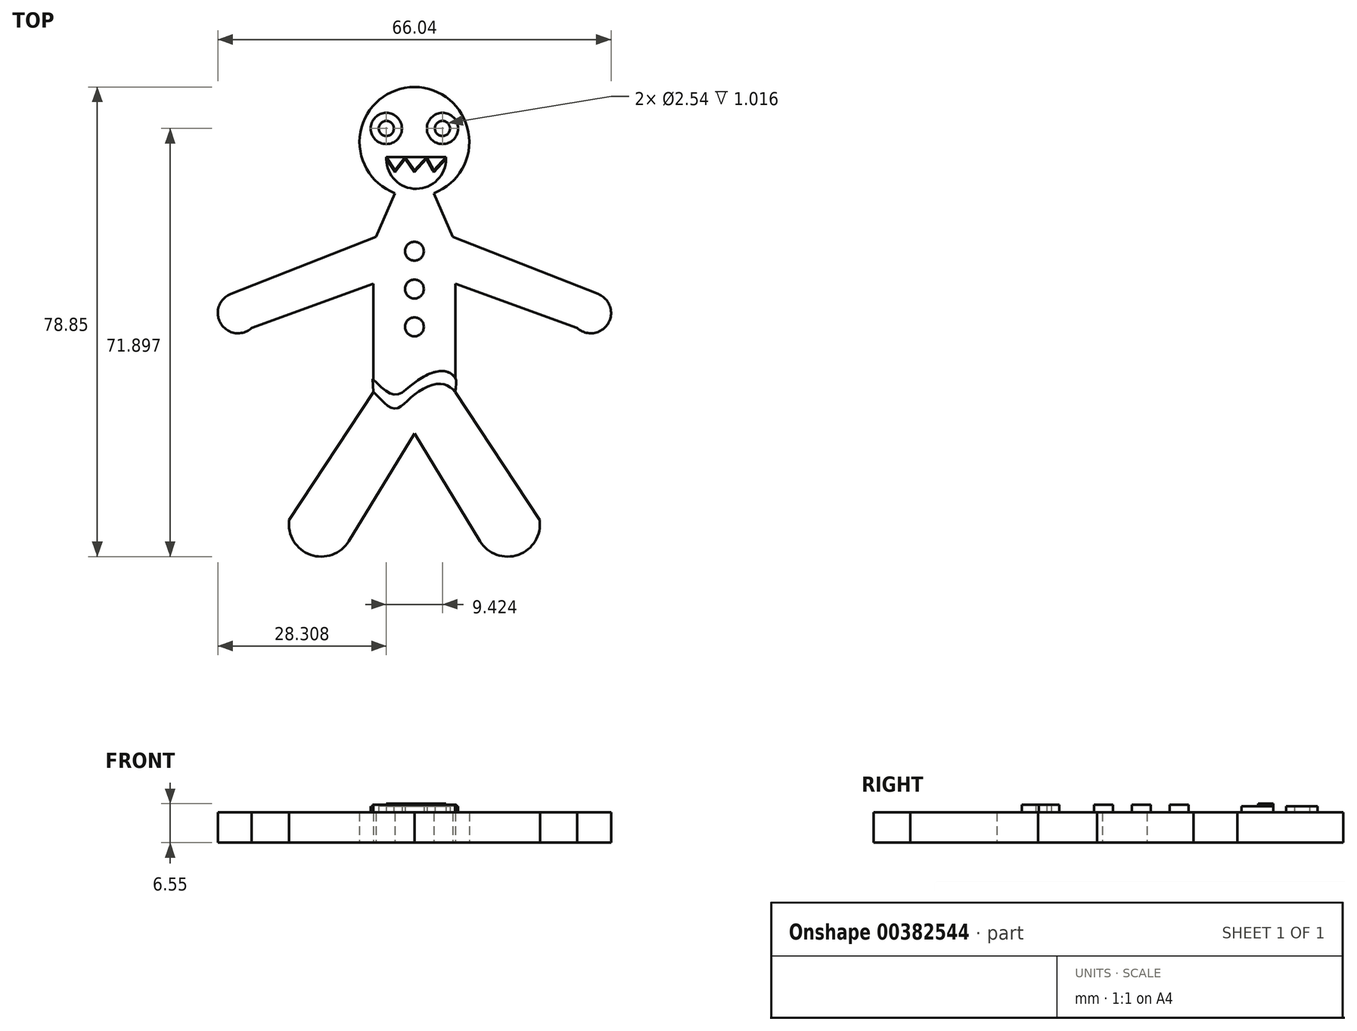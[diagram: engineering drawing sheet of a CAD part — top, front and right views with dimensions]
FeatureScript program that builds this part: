
annotation { "Feature Type Name" : "Feature", "Feature Type Description" : "" }
export const myFeature = defineFeature(function(context is Context, id is Id, definition is map)
    precondition{}
    {
        {
            var Q0;
            Q0=qCreatedBy(makeId("Top.planeOp"),FACE);
            var sketch = newSketch(context, id + "F0", { "sketchPlane" : qUnion([Q0])});
            skLineSegment(sketch, "E0", {"start": v(-6.47, 19.07) * mm, "end": v(-30.86, 9.44) * mm});
            skLineSegment(sketch, "E1", {"start": v(-27.33, 3.74) * mm, "end": v(-6.88, 11.2) * mm});
            skLineSegment(sketch, "E2", {"start": v(-6.88, 11.2) * mm, "end": v(-6.88, -7.08) * mm});
            skLineSegment(sketch, "E3", {"start": v(-6.88, -7.08) * mm, "end": v(-21.03, -28.5) * mm});
            skArc(sketch, "E4", {"start": v(-30.86, 9.44) * mm, "mid": v(-32.5, 4.47) * mm, "end": v(-27.33, 3.74) * mm});
            skLineSegment(sketch, "E5", {"start": v(0, -13.96) * mm, "end": v(-11, -32.04) * mm});
            skArc(sketch, "E6", {"start": v(-21.03, -28.5) * mm, "mid": v(-17.46, -34.34) * mm, "end": v(-11, -32.04) * mm});
            skLineSegment(sketch, "E7.MirrorCS", {"start": v(6.47, 19.07) * mm, "end": v(30.86, 9.44) * mm});
            skArc(sketch, "E8.MirrorCS", {"start": v(30.86, 9.44) * mm, "mid": v(32.5, 4.47) * mm, "end": v(27.33, 3.74) * mm});
            skLineSegment(sketch, "E9.MirrorCS", {"start": v(27.33, 3.74) * mm, "end": v(6.88, 11.2) * mm});
            skLineSegment(sketch, "E10.MirrorCS", {"start": v(6.88, 11.2) * mm, "end": v(6.88, -7.08) * mm});
            skLineSegment(sketch, "E11.MirrorCS", {"start": v(6.88, -7.08) * mm, "end": v(21.03, -28.5) * mm});
            skArc(sketch, "E12.MirrorCS", {"start": v(21.03, -28.5) * mm, "mid": v(17.46, -34.34) * mm, "end": v(11, -32.04) * mm});
            skLineSegment(sketch, "E13.MirrorCS", {"start": v(0, -13.96) * mm, "end": v(11, -32.04) * mm});
            skPoint(sketch, "E14.MirrorCS.end.orphan", {"position": v(6.47, 19.07) * mm});
            skPoint(sketch, "E15.start.orphan", {"position": v(0, 71.95) * mm});
            skLineSegment(sketch, "E16", {"start": v(-6.47, 19.07) * mm, "end": v(-3.27, 26.38) * mm});
            skLineSegment(sketch, "E17.MirrorCS", {"start": v(6.47, 19.07) * mm, "end": v(3.27, 26.38) * mm});
            skArc(sketch, "E18", {"start": v(3.27, 26.38) * mm, "mid": v(0, 44.2) * mm, "end": v(-3.27, 26.38) * mm});
            skSolve(sketch);
        }
        {
            var Q0;
            Q0 = qSketchRegion(id + "F0", true);
            extrude(context, id + "F1", {"entities" : qUnion([Q0]), "depth" : 5.08 * mm});
        }
        {
            var Q0;
            Q0=makeQuery(id+"F1.opExtrude","CAP_FACE",FACE,{"disambiguationData":[OSD([sQuery(id+"F0.wireOp",EDGE,"E0"),sQuery(id+"F0.wireOp",EDGE,"E1"),sQuery(id+"F0.wireOp",EDGE,"E2"),sQuery(id+"F0.wireOp",EDGE,"E3"),sQuery(id+"F0.wireOp",EDGE,"E4"),sQuery(id+"F0.wireOp",EDGE,"E5"),sQuery(id+"F0.wireOp",EDGE,"E6"),sQuery(id+"F0.wireOp",EDGE,"E7.MirrorCS"),sQuery(id+"F0.wireOp",EDGE,"E8.MirrorCS"),sQuery(id+"F0.wireOp",EDGE,"E9.MirrorCS"),sQuery(id+"F0.wireOp",EDGE,"E10.MirrorCS"),sQuery(id+"F0.wireOp",EDGE,"E11.MirrorCS"),sQuery(id+"F0.wireOp",EDGE,"E12.MirrorCS"),sQuery(id+"F0.wireOp",EDGE,"E13.MirrorCS"),sQuery(id+"F0.wireOp",EDGE,"E16"),sQuery(id+"F0.wireOp",EDGE,"E17.MirrorCS"),sQuery(id+"F0.wireOp",EDGE,"E18")])],"isStart":false});
            var sketch = newSketch(context, id + "F2", { "sketchPlane" : qUnion([Q0])});
            skLineSegment(sketch, "E19", {"start": v(0, 52.44) * mm, "end": v(0, -41.54) * mm, "construction": true});
            skCircle(sketch, "E20", {"center": v(-4.71, 37.25) * mm, "radius": 2.61 * mm});
            skCircle(sketch, "E21.MirrorC", {"center": v(4.71, 37.25) * mm, "radius": 2.61 * mm});
            skArc(sketch, "E22", {"start": v(-4.71, 32.45) * mm, "mid": v(0.3, 27.12) * mm, "end": v(5.3, 32.45) * mm});
            skLineSegment(sketch, "E23", {"start": v(-4.71, 32.45) * mm, "end": v(5.3, 32.45) * mm});
            skLineSegment(sketch, "E24", {"start": v(-4.71, 32.45) * mm, "end": v(-3.27, 30.24) * mm});
            skLineSegment(sketch, "E25", {"start": v(-3.27, 30.24) * mm, "end": v(-1.54, 32.45) * mm});
            skLineSegment(sketch, "E26", {"start": v(-1.54, 32.45) * mm, "end": v(0, 30.24) * mm});
            skLineSegment(sketch, "E27", {"start": v(0, 30.24) * mm, "end": v(2.03, 32.45) * mm});
            skLineSegment(sketch, "E28", {"start": v(2.03, 32.45) * mm, "end": v(3.27, 30.24) * mm});
            skLineSegment(sketch, "E29", {"start": v(3.27, 30.24) * mm, "end": v(5.3, 32.45) * mm});
            skCircle(sketch, "E30", {"center": v(4.71, 37.25) * mm, "radius": 1.27 * mm});
            skCircle(sketch, "E31", {"center": v(-4.71, 37.25) * mm, "radius": 1.27 * mm});
            skSolve(sketch);
        }
        {
            var Q0;
            Q0 = qSketchRegion(id + "F2", true);
            extrude(context, id + "F3", {"entities" : qUnion([Q0]), "operationType" : NewBodyOperationType.ADD, "depth" : 1.02 * mm});
        }
        {
            var Q0;
            Q0=makeQuery(id+"F3.opExtrude","CAP_FACE",FACE,{"disambiguationData":[OSD([sQuery(id+"F2.wireOp",EDGE,"E22"),sQuery(id+"F2.wireOp",EDGE,"E23")])],"isStart":false});
            var sketch = newSketch(context, id + "F4", { "sketchPlane" : qUnion([Q0])});
            skLineSegment(sketch, "E32.0", {"start": v(-4.71, 32.45) * mm, "end": v(-3.27, 30.24) * mm});
            skLineSegment(sketch, "E33.0", {"start": v(-3.27, 30.24) * mm, "end": v(-1.54, 32.45) * mm});
            skLineSegment(sketch, "E34.0", {"start": v(-1.54, 32.45) * mm, "end": v(0, 30.24) * mm});
            skLineSegment(sketch, "E35.0", {"start": v(0, 30.24) * mm, "end": v(2.03, 32.45) * mm});
            skLineSegment(sketch, "E36.0", {"start": v(2.03, 32.45) * mm, "end": v(3.27, 30.24) * mm});
            skLineSegment(sketch, "E37.0", {"start": v(3.27, 30.24) * mm, "end": v(5.3, 32.45) * mm});
            skLineSegment(sketch, "E38.0", {"start": v(-4.72, 32.1) * mm, "end": v(-3.44, 30.13) * mm});
            skArc(sketch, "E39.0", {"start": v(-8.9, 38.8) * mm, "mid": v(0.3, 20.77) * mm, "end": v(9.5, 38.8) * mm});
            skLineSegment(sketch, "E39.1", {"start": v(9.5, 38.8) * mm, "end": v(-8.9, 38.8) * mm});
            skLineSegment(sketch, "E40.0", {"start": v(-3.11, 30.11) * mm, "end": v(-1.55, 32.1) * mm});
            skLineSegment(sketch, "E41", {"start": v(-3.44, 30.13) * mm, "end": v(-3.29, 29.89) * mm});
            skLineSegment(sketch, "E42", {"start": v(-3.11, 30.11) * mm, "end": v(-3.29, 29.89) * mm});
            skLineSegment(sketch, "E43.0", {"start": v(-1.7, 32.34) * mm, "end": v(-1.67, 32.28) * mm});
            skLineSegment(sketch, "E44.0", {"start": v(0.15, 30.1) * mm, "end": v(2, 32.1) * mm});
            skLineSegment(sketch, "E45", {"start": v(-0.17, 30.12) * mm, "end": v(-0.02, 29.91) * mm});
            skLineSegment(sketch, "E46", {"start": v(0.15, 30.1) * mm, "end": v(-0.02, 29.91) * mm});
            skLineSegment(sketch, "E47.0", {"start": v(1.86, 32.35) * mm, "end": v(1.89, 32.3) * mm});
            skLineSegment(sketch, "E48.0", {"start": v(3.42, 30.1) * mm, "end": v(5.3, 32.16) * mm});
            skLineSegment(sketch, "E49", {"start": v(3.1, 30.14) * mm, "end": v(3.25, 29.91) * mm});
            skPoint(sketch, "E49.endSnap0", {"position": v(3.27, 29.69) * mm});
            skLineSegment(sketch, "E50", {"start": v(3.42, 30.1) * mm, "end": v(3.25, 29.91) * mm});
            skPoint(sketch, "E51.orphan", {"position": v(3.4, 29.69) * mm});
            skPoint(sketch, "E52.trimOffspring.end.orphan", {"position": v(3.27, 29.14) * mm});
            skLineSegment(sketch, "E53", {"start": v(1.86, 32.35) * mm, "end": v(1.8, 32.45) * mm});
            skLineSegment(sketch, "E54", {"start": v(2.18, 32.31) * mm, "end": v(2.31, 32.45) * mm});
            skLineSegment(sketch, "E55", {"start": v(-1.38, 32.33) * mm, "end": v(-1.28, 32.45) * mm});
            skLineSegment(sketch, "E56", {"start": v(-1.7, 32.34) * mm, "end": v(-1.8, 32.45) * mm});
            skArc(sketch, "E57.0", {"start": v(-4.71, 32.45) * mm, "mid": v(0.3, 27.12) * mm, "end": v(5.3, 32.45) * mm});
            skLineSegment(sketch, "E58.trimOffspring", {"start": v(2.14, 32.26) * mm, "end": v(2.18, 32.31) * mm});
            skLineSegment(sketch, "E59.trimOffspring", {"start": v(2, 32.1) * mm, "end": v(3.1, 30.14) * mm});
            skLineSegment(sketch, "E60.trimOffspring", {"start": v(-1.42, 32.28) * mm, "end": v(-1.38, 32.33) * mm});
            skLineSegment(sketch, "E61.trimOffspring", {"start": v(-1.55, 32.1) * mm, "end": v(-0.17, 30.12) * mm});
            skSolve(sketch);
        }
        {
            var Q0;
            {var subQ8=sQuery(id+"F4.wireOp",EDGE,"E32.0");Q0=makeQuery(id+"F4.imprint","IMPRINT",FACE,{"disambiguationData":[TD([[makeQuery(id+"F4.imprint","IMPRINT",EDGE,{"derivedFrom":subQ8}),-1.0]])]});}
            extrude(context, id + "F5", {"entities" : qUnion([Q0]), "operationType" : NewBodyOperationType.ADD, "depth" : 0.46 * mm});
        }
        {
            var Q0;
            Q0=makeQuery(id+"F2.imprint","IMPRINT",FACE,{"disambiguationData":[TD([[makeQuery(id+"F2.imprint","IMPRINT",EDGE,{"derivedFrom":sQuery(id+"F2.wireOp",EDGE,"E20")}),-1.0]])]});
            var sketch = newSketch(context, id + "F6", { "sketchPlane" : qUnion([Q0])});
            skCircle(sketch, "E62", {"center": v(0, 16.63) * mm, "radius": 1.58 * mm});
            skCircle(sketch, "E63", {"center": v(0, 10.28) * mm, "radius": 1.59 * mm});
            skCircle(sketch, "E64", {"center": v(0, 3.93) * mm, "radius": 1.59 * mm});
            skSolve(sketch);
        }
        {
            var Q0;
            Q0 = qSketchRegion(id + "F6", true);
            extrude(context, id + "F7", {"entities" : qUnion([Q0]), "operationType" : NewBodyOperationType.ADD, "depth" : 1.27 * mm});
        }
        {
            var Q0;
            Q0=makeQuery(id+"F2.imprint","IMPRINT",FACE,{"disambiguationData":[TD([[makeQuery(id+"F2.imprint","IMPRINT",EDGE,{"derivedFrom":sQuery(id+"F2.wireOp",EDGE,"E20")}),-1.0]])]});
            var sketch = newSketch(context, id + "F8", { "sketchPlane" : qUnion([Q0])});
            skFitSpline(sketch, "E65", {"points": [v(-6.87, -6.96) * mm, v(-3.23, -9.77) * mm, v(0, -7.45) * mm, v(4.54, -5.63) * mm, v(6.85, -6.96) * mm], "startDerivative": vector(14.05, -15.83) * mm, "endDerivative": vector(9.91, -9) * mm});
            skFitSpline(sketch, "E66", {"points": [v(-7.04, -4.8) * mm, v(-3.23, -7.45) * mm, v(0, -5.47) * mm, v(4.54, -3.48) * mm, v(6.85, -4.64) * mm, v(6.85, -6.96) * mm], "startDerivative": vector(17.29, -17.35) * mm, "endDerivative": vector(-3.11, -15.55) * mm});
            skFitSpline(sketch, "E67", {"points": [v(-7.04, -4.8) * mm, v(-6.87, -6.96) * mm], "startDerivative": vector(0.17, -2.15) * mm, "endDerivative": vector(0.17, -2.15) * mm});
            skSolve(sketch);
        }
        {
            var Q0;
            Q0 = qSketchRegion(id + "F8", true);
            extrude(context, id + "F9", {"entities" : qUnion([Q0]), "operationType" : NewBodyOperationType.ADD, "depth" : 1.27 * mm});
        }
    });
